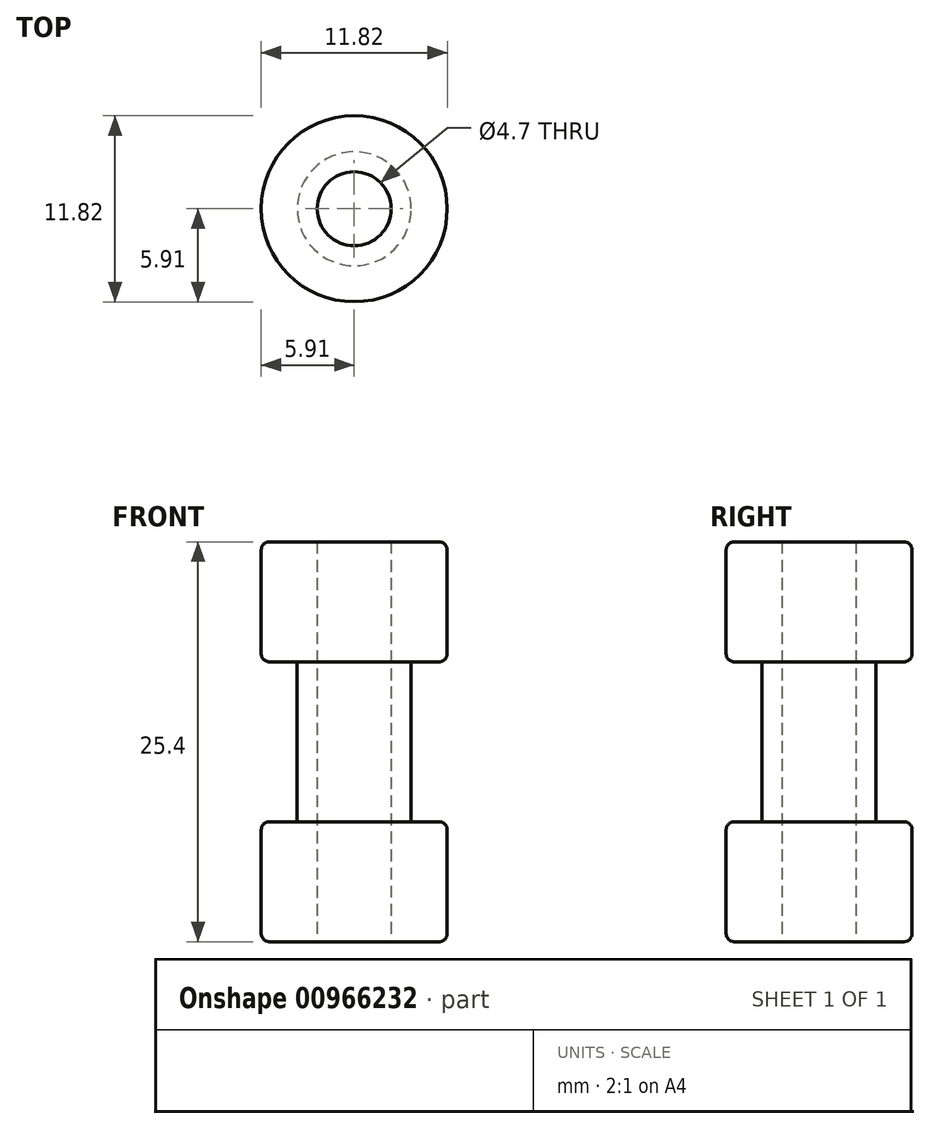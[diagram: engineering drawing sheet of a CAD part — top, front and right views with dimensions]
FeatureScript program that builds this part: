
annotation { "Feature Type Name" : "Feature", "Feature Type Description" : "" }
export const myFeature = defineFeature(function(context is Context, id is Id, definition is map)
    precondition{}
    {
        {
            var Q0;
            Q0=qCreatedBy(makeId("Front.planeOp"),FACE);
            var sketch = newSketch(context, id + "F0", { "sketchPlane" : qUnion([Q0])});
            skLineSegment(sketch, "E0", {"start": v(0, 17.85) * mm, "end": v(0, -15.24) * mm});
            skLineSegment(sketch, "E1", {"start": v(0, -15.24) * mm, "end": v(0, 17.85) * mm});
            skLineSegment(sketch, "E2", {"start": v(5.9, 17.85) * mm, "end": v(5.9, 10.23) * mm});
            skLineSegment(sketch, "E3", {"start": v(5.9, 10.23) * mm, "end": v(3.62, 10.23) * mm});
            skLineSegment(sketch, "E4", {"start": v(3.62, 10.23) * mm, "end": v(3.62, 0.07) * mm});
            skLineSegment(sketch, "E5", {"start": v(3.62, 0.07) * mm, "end": v(5.9, 0.07) * mm});
            skLineSegment(sketch, "E6", {"start": v(5.9, 0.07) * mm, "end": v(5.9, -7.55) * mm});
            skLineSegment(sketch, "E7", {"start": v(5.9, -7.55) * mm, "end": v(2.35, -7.55) * mm});
            skLineSegment(sketch, "E8", {"start": v(2.35, 17.85) * mm, "end": v(5.9, 17.85) * mm});
            skLineSegment(sketch, "E9", {"start": v(2.35, 17.85) * mm, "end": v(2.35, -7.55) * mm});
            skSolve(sketch);
        }
        {
            var Q0;
            Q0=makeQuery(id+"F0.imprint","IMPRINT",FACE,{"disambiguationData":[TD([[makeQuery(id+"F0.imprint","IMPRINT",EDGE,{"derivedFrom":sQuery(id+"F0.wireOp",EDGE,"E2")}),-1.0]])]});
            var Q1;
            Q1=sQuery(id+"F0.wireOp",EDGE,"E1");
            revolve(context, id + "F1", {"entities" : qUnion([Q0]), "axis" : qUnion([Q1]), "revolveType" : RevolveType.FULL});
        }
        {
            var Q0;
            Q0=makeQuery(id+"F1.opRevolve","SWEPT_EDGE",EDGE,{"disambiguationData":[OSD([sQuery(id+"F0.wireOp",EDGE,"E2"),sQuery(id+"F0.wireOp",EDGE,"E8")])]});
            var Q1;
            Q1=makeQuery(id+"F1.opRevolve","SWEPT_EDGE",EDGE,{"disambiguationData":[OSD([sQuery(id+"F0.wireOp",EDGE,"E2"),sQuery(id+"F0.wireOp",EDGE,"E3")])]});
            var Q2;
            Q2=makeQuery(id+"F1.opRevolve","SWEPT_EDGE",EDGE,{"disambiguationData":[OSD([sQuery(id+"F0.wireOp",EDGE,"E5"),sQuery(id+"F0.wireOp",EDGE,"E6")])]});
            fillet(context, id + "F2", {"entities" : qUnion([Q0, Q1, Q2]), "radius" : 0.5 * mm, "tangentPropagation" : true, "allowEdgeOverflow" : false});
        }
        {
            var Q0;
            Q0=makeQuery(id+"F1.opRevolve","SWEPT_EDGE",EDGE,{"disambiguationData":[OSD([sQuery(id+"F0.wireOp",EDGE,"E6"),sQuery(id+"F0.wireOp",EDGE,"E7")])]});
            fillet(context, id + "F3", {"entities" : qUnion([Q0]), "radius" : 0.5 * mm, "tangentPropagation" : true, "allowEdgeOverflow" : false});
        }
    });
